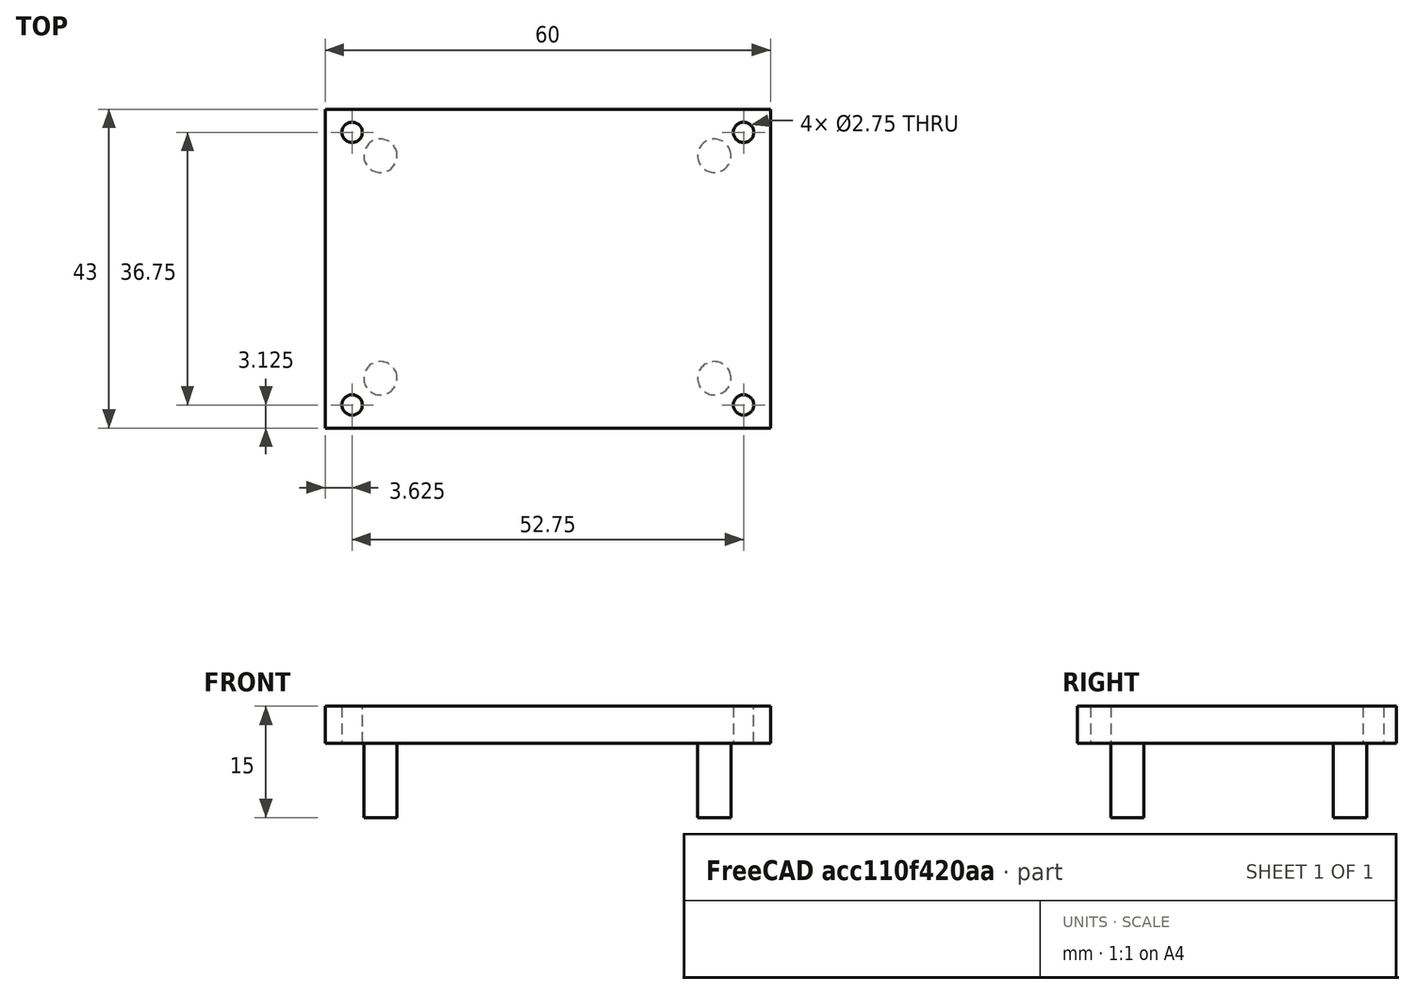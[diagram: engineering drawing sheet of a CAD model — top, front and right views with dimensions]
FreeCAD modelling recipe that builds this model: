
FCSTD DOCUMENT  (FreeCAD 1.0R39109 (Git))
Label: powerplate
License: All rights reserved
LicenseURL: https://en.wikipedia.org/wiki/All_rights_reserved
objects: Sketcher::SketchObject×2, Part::Extrusion×2, Part::Box×1, Part::Cut×1, Part::Fuse×1, Mesh::Feature×1
note: 9 computed .brp shape members not serialized (recipe doc carries the construction recipe); baked Part::Feature solids carry a one-line shape summary decoded from their .brp

FEATURE [Part::Box] Box  label="Base"
  AttacherType = Attacher::AttachEngine3D
  Height = 5
  Length = 60
  Width = 43
FEATURE [Sketcher::SketchObject] Sketch  label="Sketch-Screwholes"
  ArcFitTolerance = 1e-06
  AttachmentSupport = -> [Box]
  ExternalGeometry = -> [Box]
  FullyConstrained = true
  MakeInternals = false
  MapMode = 5
  Placement = pos=(0,0,5) rot=(0,0,1;0rad)
  sketch-geometry (4):
    g0: Circle CenterX=3.625 CenterY=39.875 CenterZ=0 NormalX=0 NormalY=0 NormalZ=1 AngleXU=0 Radius=1.375
    g1: Circle CenterX=56.375 CenterY=39.875 CenterZ=0 NormalX=0 NormalY=0 NormalZ=1 AngleXU=0 Radius=1.375
    g2: Circle CenterX=56.375 CenterY=3.125 CenterZ=0 NormalX=0 NormalY=0 NormalZ=1 AngleXU=0 Radius=1.375
    g3: Circle CenterX=3.625 CenterY=3.125 CenterZ=0 NormalX=0 NormalY=0 NormalZ=1 AngleXU=0 Radius=1.375
  constraints (12):
    c: Diameter(g0) = 2.75
    c: Diameter(g1) = 2.75
    c: Diameter(g2) = 2.75
    c: Diameter(g3) = 2.75
    c: Distance(g3,g-6) = 3.125
    c: Distance(g2,g-6) = 3.125
    c: Distance(g0,g-3) = 3.125
    c: Distance(g1,g-3) = 3.125
    c: Distance(g0,g-5) = 3.625
    c: Distance(g3,g-5) = 3.625
    c: Distance(g2,g-4) = 3.625
    c: Distance(g1,g-4) = 3.625
FEATURE [Part::Extrusion] Extrude  label="Screwholes-Negative"
  Base = -> Sketch
  Dir = (0,0,1)
  DirMode = 2
  FaceMakerClass = Part::FaceMakerBullseye
  FaceMakerMode = 3
  LengthFwd = 0
  LengthRev = 5
  Solid = true
  Symmetric = false
FEATURE [Part::Cut] Cut  label="Base-Screwholes"
  Base = -> Box
  Tool = -> Extrude
FEATURE [Sketcher::SketchObject] Sketch001  label="Sketch-Extensions"
  ArcFitTolerance = 1e-06
  AttachmentSupport = -> [Cut]
  ExternalGeometry = -> [Cut]
  FullyConstrained = true
  MakeInternals = false
  MapMode = 5
  Placement = pos=(0,0,0) rot=(1,0,0;3.14159rad)
  sketch-geometry (6):
    g0: Circle CenterX=52.4379 CenterY=-36.7235 CenterZ=0 NormalX=0 NormalY=0 NormalZ=1 AngleXU=0 Radius=2.25
    g1: Circle CenterX=7.43793 CenterY=-36.7235 CenterZ=0 NormalX=0 NormalY=0 NormalZ=1 AngleXU=0 Radius=2.25
    g2: Circle CenterX=7.43793 CenterY=-6.72349 CenterZ=0 NormalX=0 NormalY=0 NormalZ=1 AngleXU=0 Radius=2.25
    g3: Circle CenterX=52.4379 CenterY=-6.72349 CenterZ=0 NormalX=0 NormalY=0 NormalZ=1 AngleXU=0 Radius=2.25
    g4: LineSegment [constr] StartX=7.43793 StartY=-36.7235 StartZ=0 EndX=52.4379 EndY=-36.7235 EndZ=0
    g5: LineSegment [constr] StartX=7.43793 StartY=-36.7235 StartZ=0 EndX=7.43793 EndY=-6.72349 EndZ=0
  constraints (15):
    c: Diameter(g3) = 4.5
    c: Diameter(g2) = 4.5
    c: Diameter(g1) = 4.5
    c: Diameter(g0) = 4.5
    c: DistanceY(g1,g2) = 30
    c: DistanceY(g0,g3) = 30
    c: DistanceX(g1,g0) = 45
    c: DistanceX(g2,g3) = 45
    c: Coincident(g4,g1)
    c: Coincident(g4,g0)
    c: Horizontal(g4)
    c: Coincident(g5,g1)
    c: Coincident(g5,g2)
    c: Vertical(g5)
    c: Block(g2)
FEATURE [Part::Extrusion] Extrude001  label="Extensions"
  Base = -> Sketch001
  Dir = (0,0,-1)
  DirMode = 2
  FaceMakerClass = Part::FaceMakerBullseye
  FaceMakerMode = 3
  LengthFwd = 10
  LengthRev = 0
  Solid = true
  Symmetric = false
FEATURE [Part::Fuse] Fusion  label="Base-final"
  Base = -> Cut
  Tool = -> Extrude001
FEATURE [Mesh::Feature] Mesh001  label="Base-final (Meshed)001"
